# Revit family: P190780JX-119c_JGD3536GB_Black_JA_Cooking_Cooktops
name_source: partatom
category: Specialty Equipment
units: mm (PartAtom-declared; Revit-internal decimal feet)

## family parameters
Always vertical = Yes
Cut with Voids When Loaded = No
Enable Cutting in Views = No
Maintain Annotation Orientation = No
Part Type = Normal
Room Calculation Point = No
Round Connector Dimension = Use Diameter
Shared = No
Work Plane-Based = No

## types (1)
- JGD3536GB
    Amps = 0 A
    Body Material = ARCAT - Metal - Stainless Steel
    Cooking Grate Material = ARCAT - Metal - Cast Iron 1/4" Plate
    Default Elevation = 0"
    Depth = 21 1/2"
    Description = Black 36"JX3™ Gas Downdraft Cooktop
Black 36"JX3™ Gas Downdraft Cooktop
    Dimension Guide = http://access.whirlpool.com Guide&sku=JGD3536GB&language=EN
http://access.whirlpool.com Guide&sku=JGD3536GB&language=EN
    Family Name = GAS DOWNDRAFT COOKTOP - 36"
    Feature 1 = JX3™ Downdraft Ventilation System with 3 Speeds
Ventilation à évacuation descendante JX3™ à 3 vitesses
    Feature 2 = 17,000 BTU Ultra-High Output Burner
Brûleur au gaz à haute puissance de 17 000 BTU
    Feature 3 = 5,000 BTU Ultra-Low Output Burner with Melt Cap
Brûleur au gaz à faible puissance de 5000 BTU avec chapeau de brûleur
    Frame Material = ARCAT - Metal - Steel - Black
    Height = 4"
    Installation-Fabrication = http://access.whirlpool.com Instruction&sku=JGD3536GB&language=EN
http://access.whirlpool.com Instruction&sku=JGD3536GB&language=FR
    Knob Material = ARCAT - Metal - Steel - Black
    Manufacturer = Jenn Air
    Model = JGD3536GB
    Voltage = 0 V
    Width = 36"

## geometry (parser evidence)
native form markers: Sweep x3
no freeform markers — native parametric forms only
